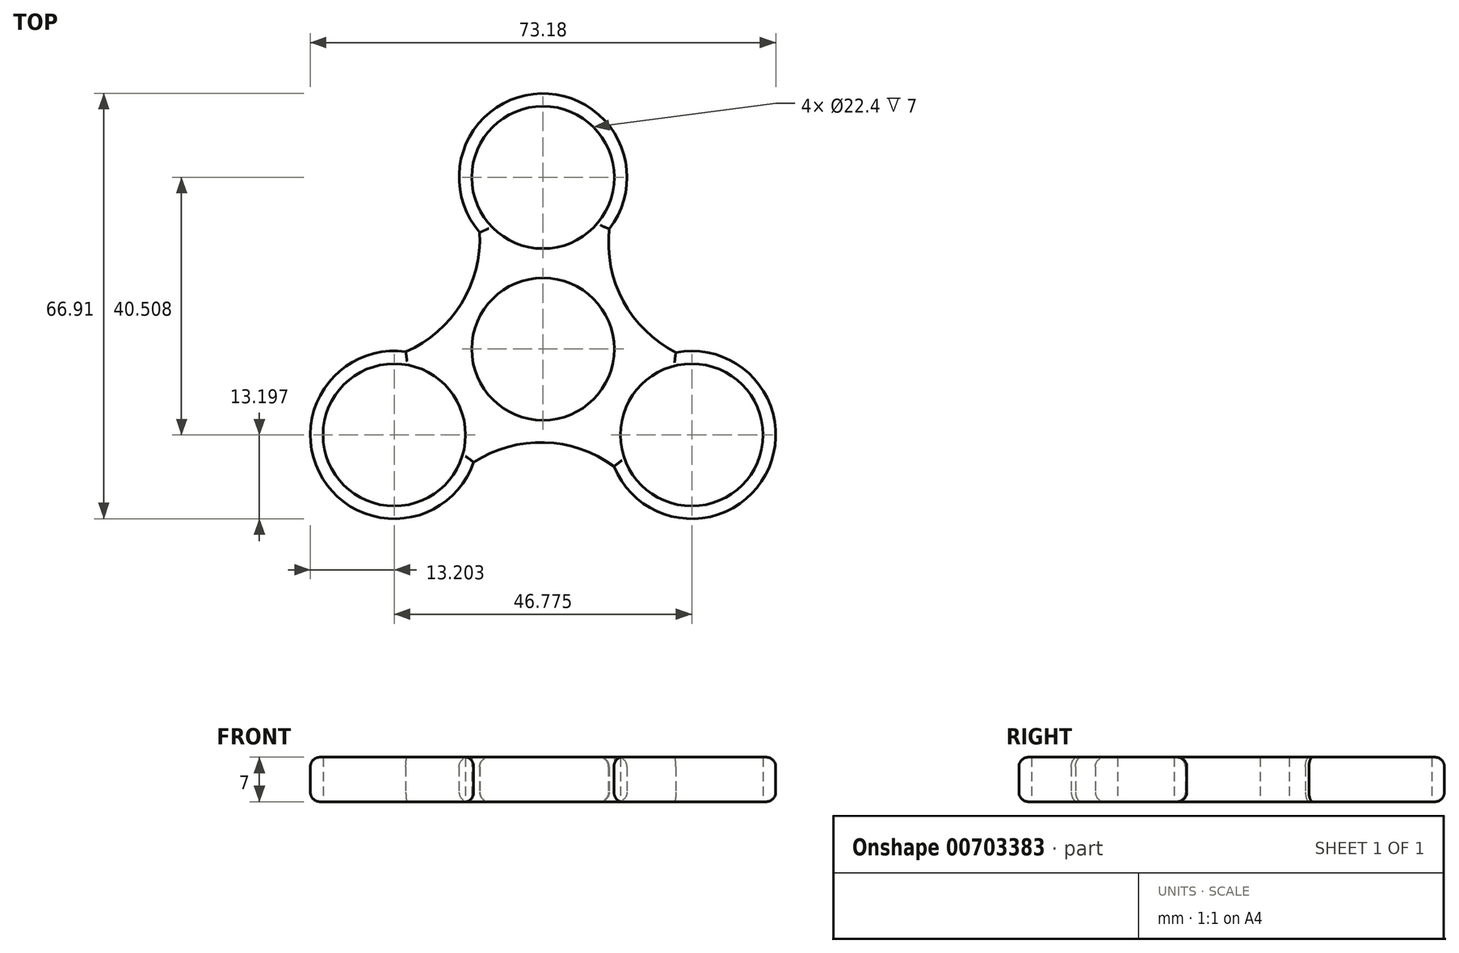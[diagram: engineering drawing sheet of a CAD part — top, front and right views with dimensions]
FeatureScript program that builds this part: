
annotation { "Feature Type Name" : "Feature", "Feature Type Description" : "" }
export const myFeature = defineFeature(function(context is Context, id is Id, definition is map)
    precondition{}
    {
        {
            var Q0;
            Q0=qCreatedBy(makeId("Top.planeOp"),FACE);
            var sketch = newSketch(context, id + "F0", { "sketchPlane" : qUnion([Q0])});
            skCircle(sketch, "E0", {"center": v(0, 0) * mm, "radius": 11.2 * mm});
            skCircle(sketch, "E1", {"center": v(0, 27) * mm, "radius": 11.2 * mm});
            skArc(sketch, "E2", {"start": v(10.42, 18.9) * mm, "mid": v(-0.35, 40.2) * mm, "end": v(-9.97, 18.35) * mm});
            skCircle(sketch, "E3.1.0", {"center": v(-23.39, -13.5) * mm, "radius": 11.2 * mm});
            skArc(sketch, "E3.1.1", {"start": v(-21.57, -0.43) * mm, "mid": v(-34.64, -20.4) * mm, "end": v(-10.9, -17.8) * mm});
            skCircle(sketch, "E3.2.0", {"center": v(23.39, -13.5) * mm, "radius": 11.2 * mm});
            skArc(sketch, "E3.2.1", {"start": v(11.16, -18.47) * mm, "mid": v(35, -19.8) * mm, "end": v(20.88, -0.54) * mm});
            skArc(sketch, "E4", {"start": v(10.42, 18.9) * mm, "mid": v(12.61, 7.54) * mm, "end": v(20.88, -0.54) * mm});
            skArc(sketch, "E5.1.0", {"start": v(-21.57, -0.43) * mm, "mid": v(-12.84, 7.15) * mm, "end": v(-9.97, 18.35) * mm});
            skArc(sketch, "E5.2.0", {"start": v(11.16, -18.47) * mm, "mid": v(0.23, -14.7) * mm, "end": v(-10.9, -17.8) * mm});
            skSolve(sketch);
        }
        {
            var Q0;
            Q0=makeQuery(id+"F0.imprint","IMPRINT",FACE,{"disambiguationData":[TD([[makeQuery(id+"F0.imprint","IMPRINT",EDGE,{"derivedFrom":sQuery(id+"F0.wireOp",EDGE,"E0")}),-1.0]])]});
            extrude(context, id + "F1", {"entities" : qUnion([Q0]), "depth" : 7 * mm, "offsetDistance" : 25 * mm});
        }
        {
            var Q0;
            Q0=makeQuery(id+"F1.opExtrude","CAP_EDGE",EDGE,{"disambiguationData":[OSD([sQuery(id+"F0.wireOp",EDGE,"E5.2.0")])],"isStart":false});
            var Q1;
            Q1=makeQuery(id+"F1.opExtrude","CAP_EDGE",EDGE,{"disambiguationData":[OSD([sQuery(id+"F0.wireOp",EDGE,"E5.2.0")])],"isStart":true});
            var Q2;
            Q2=makeQuery(id+"F1.opExtrude","CAP_EDGE",EDGE,{"disambiguationData":[OSD([sQuery(id+"F0.wireOp",EDGE,"E4")])],"isStart":false});
            var Q3;
            Q3=makeQuery(id+"F1.opExtrude","CAP_EDGE",EDGE,{"disambiguationData":[OSD([sQuery(id+"F0.wireOp",EDGE,"E4")])],"isStart":true});
            var Q4;
            Q4=makeQuery(id+"F1.opExtrude","CAP_EDGE",EDGE,{"disambiguationData":[OSD([sQuery(id+"F0.wireOp",EDGE,"E5.1.0")])],"isStart":false});
            var Q5;
            Q5=makeQuery(id+"F1.opExtrude","CAP_EDGE",EDGE,{"disambiguationData":[OSD([sQuery(id+"F0.wireOp",EDGE,"E5.1.0")])],"isStart":true});
            var Q6;
            Q6=makeQuery(id+"F1.opExtrude","CAP_EDGE",EDGE,{"disambiguationData":[OSD([sQuery(id+"F0.wireOp",EDGE,"E3.1.1")])],"isStart":false});
            var Q7;
            Q7=makeQuery(id+"F1.opExtrude","CAP_EDGE",EDGE,{"disambiguationData":[OSD([sQuery(id+"F0.wireOp",EDGE,"E3.2.1")])],"isStart":false});
            var Q8;
            Q8=makeQuery(id+"F1.opExtrude","CAP_EDGE",EDGE,{"disambiguationData":[OSD([sQuery(id+"F0.wireOp",EDGE,"E2")])],"isStart":false});
            fillet(context, id + "F2", {"entities" : qUnion([Q0, Q1, Q2, Q3, Q4, Q5, Q6, Q7, Q8]), "radius" : 1.5 * mm, "tangentPropagation" : true, "allowEdgeOverflow" : false});
        }
        {
            var Q0;
            Q0=makeQuery(id+"F1.opExtrude","CAP_EDGE",EDGE,{"disambiguationData":[OSD([sQuery(id+"F0.wireOp",EDGE,"E3.2.1")])],"isStart":true});
            var Q1;
            Q1=makeQuery(id+"F1.opExtrude","CAP_EDGE",EDGE,{"disambiguationData":[OSD([sQuery(id+"F0.wireOp",EDGE,"E2")])],"isStart":true});
            var Q2;
            Q2=makeQuery(id+"F1.opExtrude","CAP_EDGE",EDGE,{"disambiguationData":[OSD([sQuery(id+"F0.wireOp",EDGE,"E3.1.1")])],"isStart":true});
            fillet(context, id + "F3", {"entities" : qUnion([Q0, Q1, Q2]), "radius" : 1.5 * mm, "tangentPropagation" : true, "allowEdgeOverflow" : false});
        }
    });
